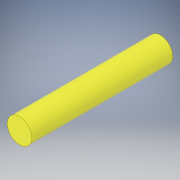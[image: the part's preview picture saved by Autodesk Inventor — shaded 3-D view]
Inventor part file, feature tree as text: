
AUTODESK INVENTOR PART (.ipt)
format: ipt  version: 2019 (Build 230136000, 136)  size: 99,328 bytes
history: native  units: mm
features: extrude x1, sketch x1
ambient origin geometry x8: Origin, YZ Plane, XZ Plane, XY Plane, X Axis, Y Axis, Z Axis, Center Point
bodies: Solid1 (feature_tree)
feature tree (2):
  extrude  "Extrusion1"  Depth=20.0mm TaperAngle=0.0deg
  sketch  "Sketch1"  dims[d0=3.5mm d1=20.0mm d2=0.0mm]
